# Revit family: IS_SeptaPro_R0139_BIM_DE
name_source: partatom
category: Plumbing Fixtures
revit_build: Autodesk Revit 2017 (Build: 20160225_1515(x64)
units: mm (PartAtom-declared; Revit-internal decimal feet)

## family parameters
Cut with Voids When Loaded = No
Host = Face
OmniClass Number = 23.45.05.21.11.11
OmniClass Title = Water Operated Water Closets
Part Type = Normal
Room Calculation Point = No
Round Connector Dimension = Use Diameter
Shared = Yes

## types (3) — shared parameters
Accesoires = https://www.idealstandard.de
Afmetingen = 250 x 391 x 595 mm
AfstandsEenheid = Millimeter
Assembly Code = C1030200
Auteur = Ideal Standrad
Beschrijvinggarantie = Garantie van de fabrikant
BimObjectNaam = IS_IdealStandard_WCcisternflushpipes_SeptaPro_R0139
Diepte = 391 mm
Douchebak = No
DuurEenheid = Jaren
Garantieonderdelen = 5
Garantieunits = Jaren
Heefthandvaten = No
Hoogte = 250
Hulp = https://www.idealstandard.de
Installatieinstructies = https://www.idealstandard.de
Manufacturer = https://www.idealstandard.de
Materiaal = Metall
Merk = Ideal Standard
Montageinstuctie = https://www.idealstandard.de
NBSDescription = WC cistern flush pipes
NBSReference = 45-35-70/388
Normen = WCcisternflushpipes_SeptaPro_R0139_IdealStandard
Productinformatie = https://www.idealstandard.de
Revisie = 1
Revision = 1
Telefoonnummer = 0049 228 5210
URL = https://www.idealstandard.de
Uniclass2 = Pr_40_20_93_89
Uniclass2015Beschrijving = WC cistern flush pipes
Uniclass2015Description = WC cistern flush pipes
Uniclass2015Reference = Pr_40_20_93_90
Uniclass2015Referentie = Pr_40_20_93_90
Urlproducent = https://www.idealstandard.de
Versie = 1
Verwachtelevensduur = 25
Volumeunits = liter
WRAS = No
WaterEfficientProduct = No
zero-valued in all types: Breedte, BrutoGewicht, CWFU, Cost, Default Elevation, GrootteAfvoergat, HWFU, Lengte, Nettogewicht, Overloop, Vervangingskosten, WFU

## per-type parameters (varying)
| type | Afwerking | Artikelnummer | Artikelomschrijving | Artikelreferentie | Barcode | Description | Eigenschappen | Kleur | Model | Referentie |
| R0139AC - SEPTA PRO U3 F/PLATE WHITE | White | R0139AC | Betätigungsplatte SEPTA PRO. f.Urinal. Weiß | Betätigungsplatte SEPTA PRO. f.Urinal. Weiß | 3391500580701 | Betätigungsplatte SEPTA PRO. f.Urinal. Weiß | Betätigungsplatte . f.Urinal. Weiß | Weiß | R0139AC | R0139AC |
| R0139AA - SEPTA PRO U3 F/PLATE CHROME | Chrome | R0139AA | Betätigungsplatte SEPTA PRO. f.Urinal. Chrom | Betätigungsplatte SEPTA PRO. f.Urinal. Chrom | 3391500580695 | Betätigungsplatte SEPTA PRO. f.Urinal. Chrom | Betätigungsplatte . f.Urinal. Chrom | Chrom | R0139AA | R0139AA |
| R0139JG - SEPTA PRO U3 F/PLATE MATT CHROME | Matt Chrome | R0139JG | Betätigungsplatte SEPTA PRO. f.Urinal. Chrom matt | Betätigungsplatte SEPTA PRO. f.Urinal. Chrom matt | 3391500580718 | Betätigungsplatte SEPTA PRO. f.Urinal. Chrom matt | Betätigungsplatte . f.Urinal. Chrom matt | Mat chroom | R0139JG | R0139JG |

## geometry (parser evidence)
native form markers: Sweep x3
no freeform markers — native parametric forms only
